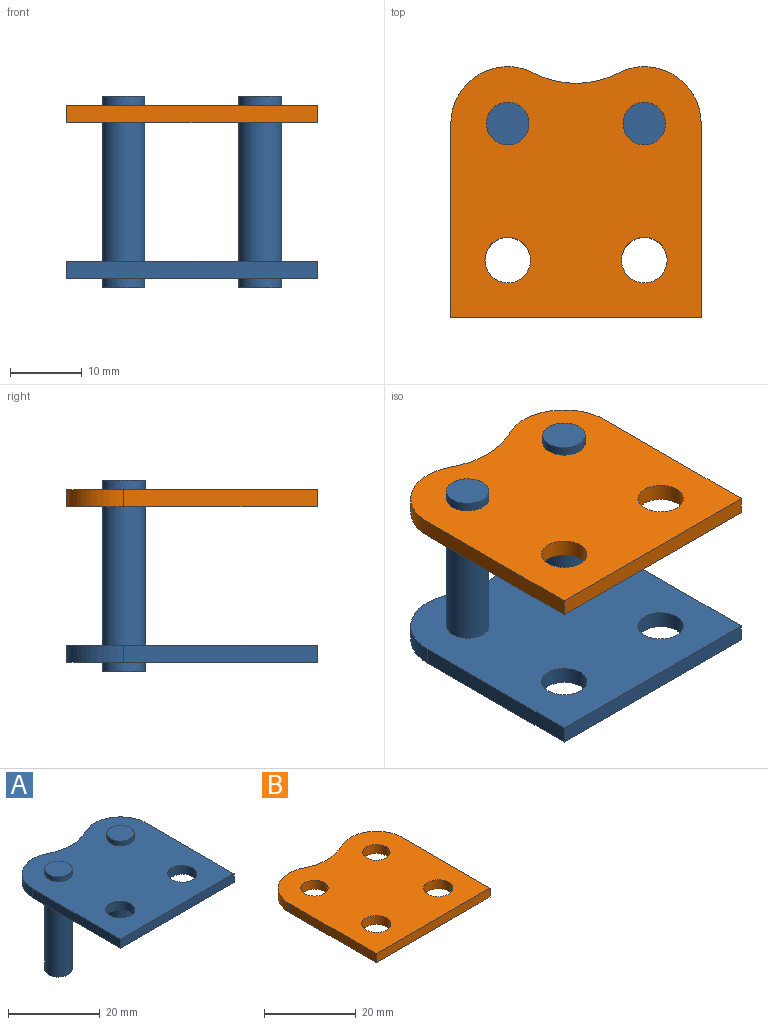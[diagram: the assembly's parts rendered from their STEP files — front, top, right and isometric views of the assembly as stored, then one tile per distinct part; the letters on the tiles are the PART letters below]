
ASSEMBLY  parts=2 mates=1
PART A: 18 faces, bbox 34.9x34.9x26.7 mm
  f0: plane 26.99x2.38mm, normal (1,0,0), area 64.3mm2, adj f1,f5,f6,f7
  f1: cylinder r=7.94mm len=11.6mm, axis (0,0,-1), area 38.8mm2, adj f0,f2,f6,f7
  f2: cylinder r=12.7mm len=11.72mm, axis (0,0,-1), area 29mm2, adj f1,f3,f6,f7
  f3: cylinder r=7.94mm len=11.6mm, axis (0,0,-1), area 38.8mm2, adj f2,f4,f6,f7
  f4: plane 26.99x2.38mm, normal (-1,0,0), area 64.3mm2, adj f3,f5,f6,f7
  f5: plane 34.93x2.38mm, normal (0,-1,0), area 83.2mm2, adj f0,f4,f6,f7
  f6: plane 34.93x34.93mm, normal (0,0,1), area 1049.9mm2, adj f0,f1,f2,f3,f4,f5,f8,f9
  f7: plane 34.93x34.93mm, normal (0,0,-1), area 1049.9mm2, adj f0,f1,f2,f3,f4,f5,f8,f9
  f8: cylinder r=3.17mm len=6.35mm, axis (0,0,1), area 47.5mm2, adj f6,f7
  f9: cylinder r=3.17mm len=6.35mm, axis (0,0,1), area 47.5mm2, adj f6,f7
  f10: plane 5.94x5.94mm, normal (0,0,-1), area 27.7mm2, adj f11
  f11: cylinder r=2.97mm len=23.02mm, axis (0,0,-1), area 429.8mm2, adj f7,f10
  f12: cylinder r=2.97mm len=5.94mm, axis (0,0,-1), area 23.7mm2, adj f6,f13
  f13: plane 5.94x5.94mm, normal (0,0,1), area 27.7mm2, adj f12
  f14: plane 5.94x5.94mm, normal (0,0,-1), area 27.7mm2, adj f15
  f15: cylinder r=2.97mm len=23.02mm, axis (0,0,-1), area 429.8mm2, adj f7,f14
  f16: cylinder r=2.97mm len=5.94mm, axis (0,0,-1), area 23.7mm2, adj f6,f17
  f17: plane 5.94x5.94mm, normal (0,0,1), area 27.7mm2, adj f16
PART B: 12 faces, bbox 34.9x34.9x2.4 mm
  f0: plane 26.99x2.38mm, normal (1,0,0), area 64.3mm2, adj f1,f5,f6,f7
  f1: cylinder r=7.94mm len=11.6mm, axis (0,0,-1), area 38.8mm2, adj f0,f2,f6,f7
  f2: cylinder r=12.7mm len=11.72mm, axis (0,0,-1), area 29mm2, adj f1,f3,f6,f7
  f3: cylinder r=7.94mm len=11.6mm, axis (0,0,-1), area 38.8mm2, adj f2,f4,f6,f7
  f4: plane 26.99x2.38mm, normal (-1,0,0), area 64.3mm2, adj f3,f5,f6,f7
  f5: plane 34.93x2.38mm, normal (0,-1,0), area 83.2mm2, adj f0,f4,f6,f7
  f6: plane 34.93x34.93mm, normal (0,0,1), area 1049.9mm2, adj f0,f1,f2,f3,f4,f5,f8,f9
  f7: plane 34.93x34.93mm, normal (0,0,-1), area 1049.9mm2, adj f0,f1,f2,f3,f4,f5,f8,f9
  f8: cylinder r=2.97mm len=5.94mm, axis (0,0,1), area 44.5mm2, adj f6,f7
  f9: cylinder r=2.97mm len=5.94mm, axis (0,0,1), area 44.5mm2, adj f6,f7
  f10: cylinder r=3.17mm len=6.35mm, axis (0,0,1), area 47.5mm2, adj f6,f7
  f11: cylinder r=3.17mm len=6.35mm, axis (0,0,1), area 47.5mm2, adj f6,f7
PLACE A rot(axis=(0,-1,0),180deg) t=(0,-3.26,2.38)mm
PLACE B rot(axis=(0,-1,0),180deg) t=(0,-3.26,24.13)mm
MATE fastened B.f8 <-> A.f11  axis (0,0,1) through (9.53,10.24,24.13)mm
